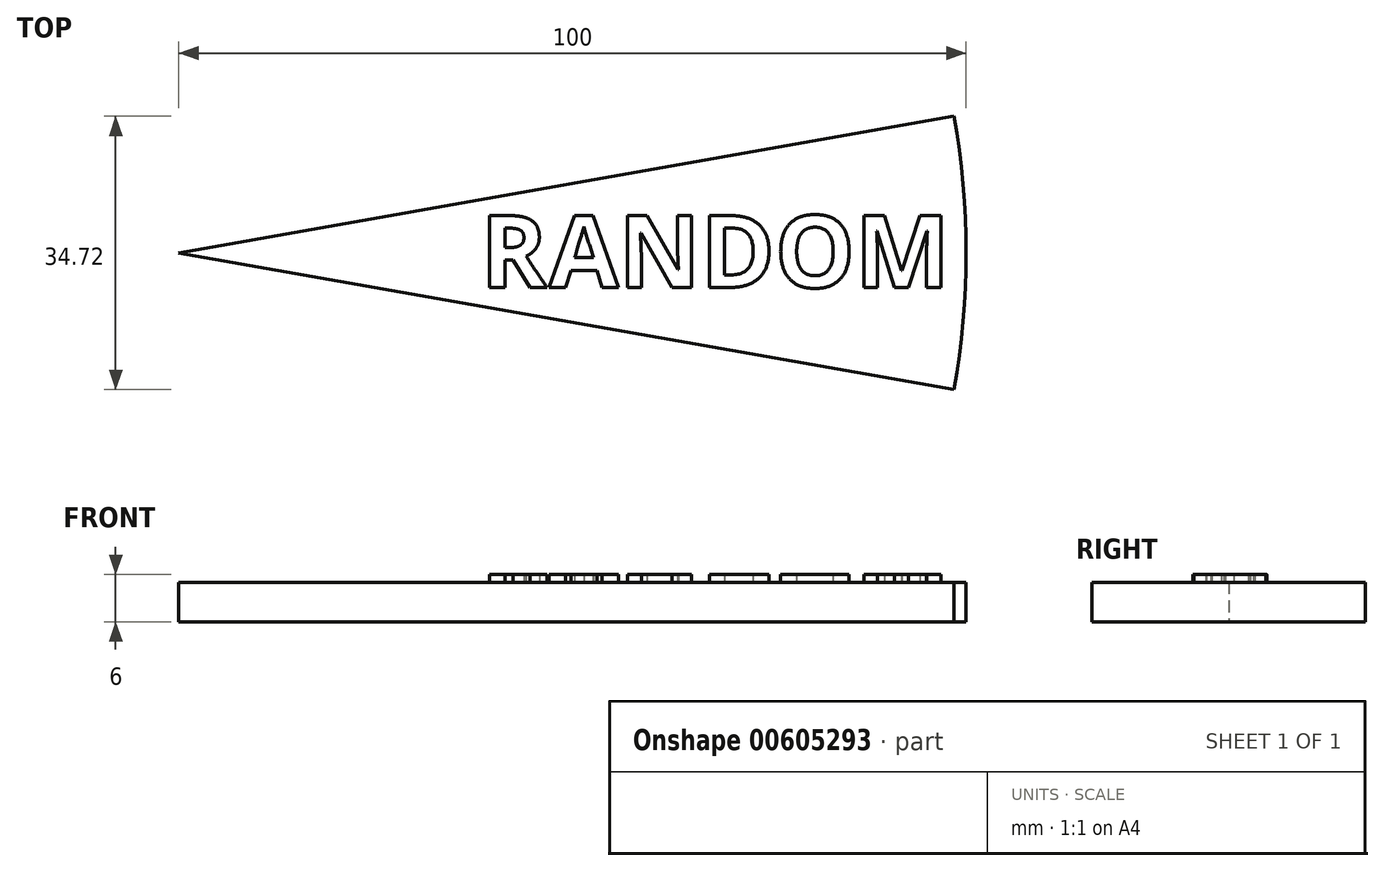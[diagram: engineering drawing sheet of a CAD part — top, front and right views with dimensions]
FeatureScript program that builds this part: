
annotation { "Feature Type Name" : "Feature", "Feature Type Description" : "" }
export const myFeature = defineFeature(function(context is Context, id is Id, definition is map)
    precondition{}
    {
        {
            var Q0;
            Q0=qCreatedBy(makeId("Top.planeOp"),FACE);
            var sketch = newSketch(context, id + "F0", { "sketchPlane" : qUnion([Q0])});
            skArc(sketch, "E0", {"start": v(98.48, -17.36) * mm, "mid": v(100, 0) * mm, "end": v(98.48, 17.36) * mm});
            skLineSegment(sketch, "E1", {"start": v(0, 0) * mm, "end": v(100, 0) * mm});
            skLineSegment(sketch, "E2", {"start": v(0, 0) * mm, "end": v(98.48, 17.36) * mm});
            skLineSegment(sketch, "E3", {"start": v(0, 0) * mm, "end": v(98.48, -17.36) * mm});
            skSolve(sketch);
        }
        {
            var Q0;
            Q0=qSketchRegion(id+"F0",true);
            extrude(context, id + "F1", {"entities" : qUnion([Q0]), "depth" : 5 * mm, "offsetDistance" : 25 * mm});
        }
        {
            var Q0;
            Q0=makeQuery(id+"F1.opExtrude","CAP_FACE",FACE,{"disambiguationData":[OSD([sQuery(id+"F0.wireOp",EDGE,"E0"),sQuery(id+"F0.wireOp",EDGE,"E2"),sQuery(id+"F0.wireOp",EDGE,"E3")])],"isStart":false});
            var sketch = newSketch(context, id + "F2", { "sketchPlane" : qUnion([Q0])});
            skText(sketch, "E4", { "text": "RANDOM", "fontName": "OpenSans-Bold.ttf"});
            const initialGuessF2  = {"E4": [0.03834, -0.0044, 1, 0, 0.0092]};
            skSetInitialGuess(sketch, initialGuessF2);
            skSolve(sketch);
        }
        {
            var Q0;
            Q0 = qSketchRegion(id + "F2", true);
            extrude(context, id + "F3", {"entities" : qUnion([Q0]), "operationType" : NewBodyOperationType.ADD, "depth" : 1 * mm, "offsetDistance" : 25 * mm});
        }
    });
